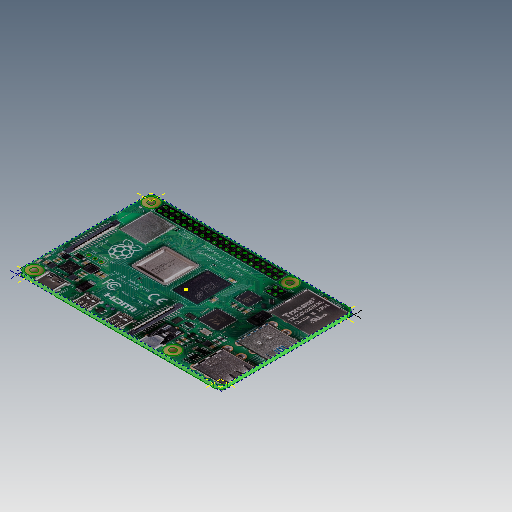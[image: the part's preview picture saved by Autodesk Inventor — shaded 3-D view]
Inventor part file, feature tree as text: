
AUTODESK INVENTOR PART (.ipt)
format: ipt  version: 2020 (Build 240168000, 168)  size: 1,793,536 bytes
history: native  units: in
note: dims shown in document units (in); Inventor stores cm internally (conversion verified against a paired STEP export)
features: other x3, sketch x2
ambient origin geometry x8: Origin, YZ Plane, XZ Plane, XY Plane, X Axis, Y Axis, Z Axis, Center Point
bodies: Solid1 (feature_tree)
feature tree (5):
  sketch  "Sketch3"
  sketch  "Sketch4"
  other  "Image3"
  other  "Image4"
  other  "CornerRadius"
